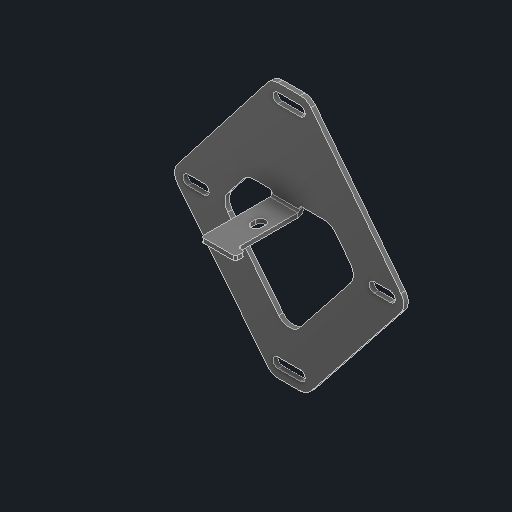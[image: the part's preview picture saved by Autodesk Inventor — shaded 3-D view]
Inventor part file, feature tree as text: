
AUTODESK INVENTOR PART (.ipt)
format: ipt  version: 2024 (Build 280153000, 153)  size: 143,360 bytes
history: native  units: in
note: dims shown in document units (in); Inventor stores cm internally (conversion verified against a paired STEP export)
features: fillet x1
ambient origin geometry x8: Origin, YZ Plane, XZ Plane, XY Plane, X Axis, Y Axis, Z Axis, Center Point
bodies: Solid1 (feature_tree)
feature tree (1):
  fillet  "Fillet2"  [1 undecoded]
note: 1 required parameter value undecoded (feature->parameter linkage not recoverable at this tier; creation-order binding heuristic only, values carry confidence <= 0.55)
